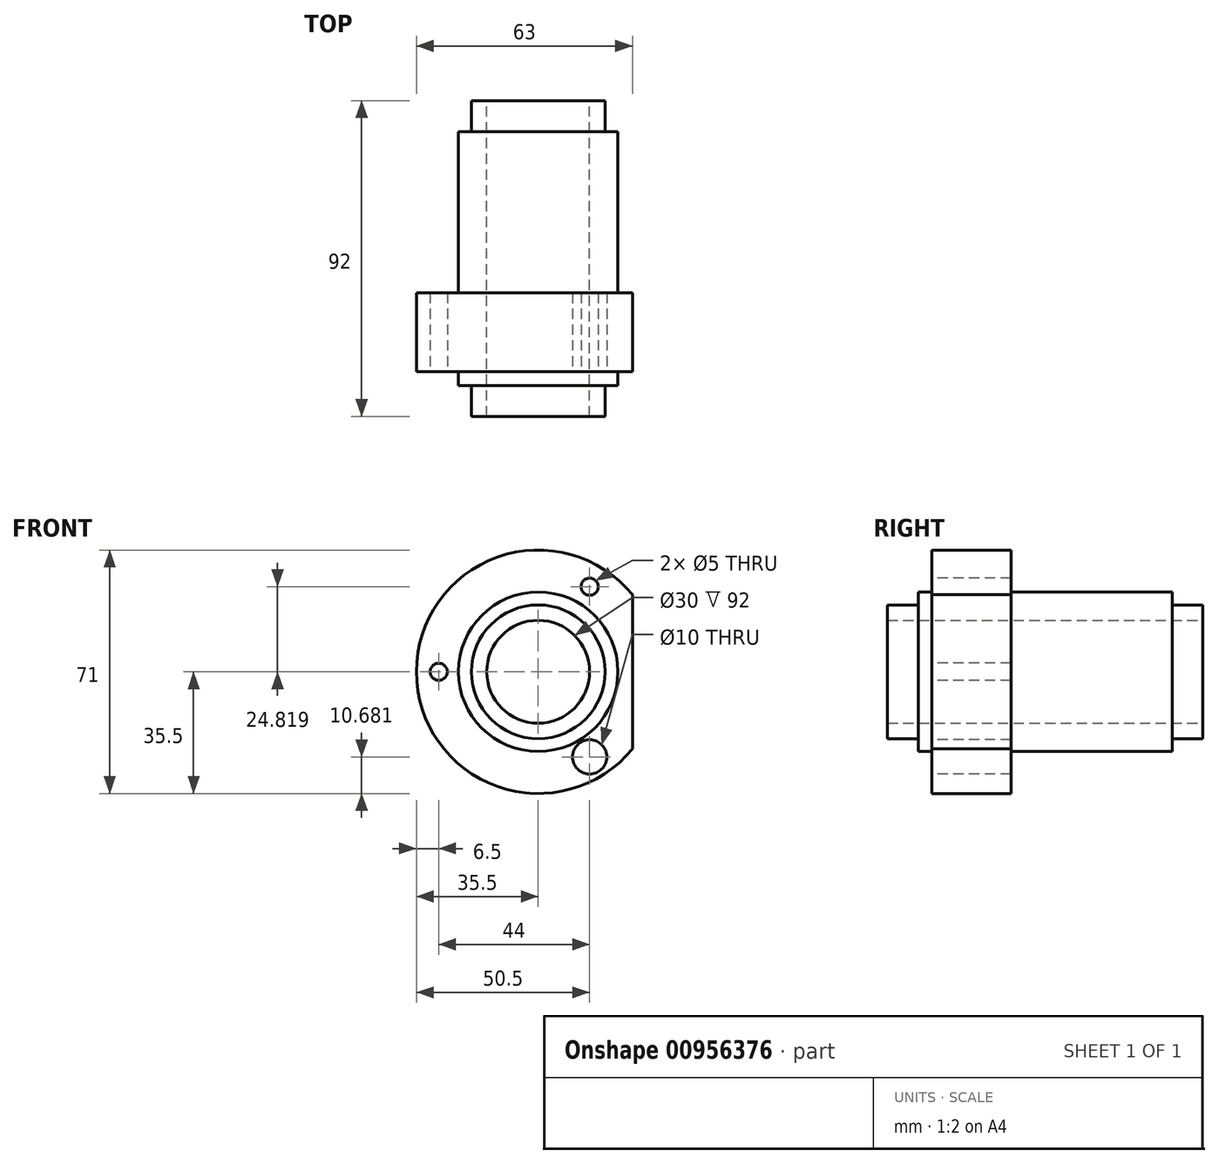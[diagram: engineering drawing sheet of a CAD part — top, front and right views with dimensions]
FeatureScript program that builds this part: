
annotation { "Feature Type Name" : "Feature", "Feature Type Description" : "" }
export const myFeature = defineFeature(function(context is Context, id is Id, definition is map)
    precondition{}
    {
        {
            var Q0;
            Q0=qCreatedBy(makeId("Front.planeOp"),FACE);
            var sketch = newSketch(context, id + "F0", { "sketchPlane" : qUnion([Q0])});
            skCircle(sketch, "E0", {"center": v(0, 0) * mm, "radius": 35.5 * mm});
            skCircle(sketch, "E1", {"center": v(0, 0) * mm, "radius": 15 * mm});
            skCircle(sketch, "E2", {"center": v(0, 0) * mm, "radius": 19.5 * mm});
            skCircle(sketch, "E3", {"center": v(0, 0) * mm, "radius": 23.25 * mm});
            skLineSegment(sketch, "E4", {"start": v(27.5, 22.45) * mm, "end": v(27.5, -22.45) * mm});
            skCircle(sketch, "E5", {"center": v(15, 24.82) * mm, "radius": 5 * mm});
            skCircle(sketch, "E6", {"center": v(15, 24.82) * mm, "radius": 2.5 * mm});
            skCircle(sketch, "E7", {"center": v(-29, 0) * mm, "radius": 5 * mm});
            skCircle(sketch, "E8", {"center": v(-29, 0) * mm, "radius": 2.5 * mm});
            skCircle(sketch, "E9.MirrorC", {"center": v(15, -24.82) * mm, "radius": 5 * mm});
            skCircle(sketch, "E10.MirrorC", {"center": v(15, -24.82) * mm, "radius": 2.5 * mm});
            skSolve(sketch);
        }
        {
            var Q0;
            Q0=makeQuery(id+"F0.imprint","IMPRINT",FACE,{"disambiguationData":[TD([[makeQuery(id+"F0.imprint","IMPRINT",EDGE,{"derivedFrom":sQuery(id+"F0.wireOp",EDGE,"E1")}),-1.0]])]});
            extrude(context, id + "F1", {"entities" : qUnion([Q0]), "depth" : 9 * mm, "offsetDistance" : 25.4 * mm});
        }
        {
            var Q0;
            Q0=makeQuery(id+"F0.imprint","IMPRINT",FACE,{"disambiguationData":[TD([[makeQuery(id+"F0.imprint","IMPRINT",EDGE,{"derivedFrom":sQuery(id+"F0.wireOp",EDGE,"E1")}),-1.0]])]});
            extrude(context, id + "F2", {"entities" : qUnion([Q0]), "operationType" : NewBodyOperationType.ADD, "oppositeDirection" : true, "depth" : 83 * mm, "offsetDistance" : 25.4 * mm});
        }
        {
            var Q0;
            Q0=makeQuery(id+"F0.imprint","IMPRINT",FACE,{"disambiguationData":[TD([[makeQuery(id+"F0.imprint","IMPRINT",EDGE,{"derivedFrom":sQuery(id+"F0.wireOp",EDGE,"E2")}),-1.0]])]});
            extrude(context, id + "F3", {"entities" : qUnion([Q0]), "operationType" : NewBodyOperationType.ADD, "oppositeDirection" : true, "depth" : 74 * mm, "offsetDistance" : 25.4 * mm});
        }
        {
            var Q0;
            Q0=makeQuery(id+"F0.imprint","IMPRINT",FACE,{"disambiguationData":[TD([[makeQuery(id+"F0.imprint","IMPRINT",EDGE,{"derivedFrom":sQuery(id+"F0.wireOp",EDGE,"E3")}),-1.0]])]});
            var Q1;
            Q1=makeQuery(id+"F0.imprint","IMPRINT",FACE,{"disambiguationData":[TD([[makeQuery(id+"F0.imprint","IMPRINT",EDGE,{"derivedFrom":sQuery(id+"F0.wireOp",EDGE,"E5")}),1.0]])]});
            var Q2;
            Q2=makeQuery(id+"F0.imprint","IMPRINT",FACE,{"disambiguationData":[TD([[makeQuery(id+"F0.imprint","IMPRINT",EDGE,{"derivedFrom":sQuery(id+"F0.wireOp",EDGE,"E6")}),1.0]])]});
            var Q3;
            Q3=makeQuery(id+"F0.imprint","IMPRINT",FACE,{"disambiguationData":[TD([[makeQuery(id+"F0.imprint","IMPRINT",EDGE,{"derivedFrom":sQuery(id+"F0.wireOp",EDGE,"E9.MirrorC")}),-1.0]])]});
            var Q4;
            Q4=makeQuery(id+"F0.imprint","IMPRINT",FACE,{"disambiguationData":[TD([[makeQuery(id+"F0.imprint","IMPRINT",EDGE,{"derivedFrom":sQuery(id+"F0.wireOp",EDGE,"E10.MirrorC")}),-1.0]])]});
            var Q5;
            Q5=makeQuery(id+"F0.imprint","IMPRINT",FACE,{"disambiguationData":[TD([[makeQuery(id+"F0.imprint","IMPRINT",EDGE,{"derivedFrom":sQuery(id+"F0.wireOp",EDGE,"E7")}),1.0]])]});
            var Q6;
            Q6=makeQuery(id+"F0.imprint","IMPRINT",FACE,{"disambiguationData":[TD([[makeQuery(id+"F0.imprint","IMPRINT",EDGE,{"derivedFrom":sQuery(id+"F0.wireOp",EDGE,"E8")}),1.0]])]});
            extrude(context, id + "F4", {"entities" : qUnion([Q0, Q1, Q2, Q3, Q4, Q5, Q6]), "operationType" : NewBodyOperationType.ADD, "oppositeDirection" : true, "depth" : 27 * mm, "offsetDistance" : 25.4 * mm});
        }
        {
            var Q0;
            Q0=makeQuery(id+"F0.imprint","IMPRINT",FACE,{"disambiguationData":[TD([[makeQuery(id+"F0.imprint","IMPRINT",EDGE,{"derivedFrom":sQuery(id+"F0.wireOp",EDGE,"E9.MirrorC")}),-1.0]])]});
            var Q1;
            Q1=makeQuery(id+"F0.imprint","IMPRINT",FACE,{"disambiguationData":[TD([[makeQuery(id+"F0.imprint","IMPRINT",EDGE,{"derivedFrom":sQuery(id+"F0.wireOp",EDGE,"E5")}),1.0]])]});
            var Q2;
            Q2=makeQuery(id+"F0.imprint","IMPRINT",FACE,{"disambiguationData":[TD([[makeQuery(id+"F0.imprint","IMPRINT",EDGE,{"derivedFrom":sQuery(id+"F0.wireOp",EDGE,"E7")}),1.0]])]});
            extrude(context, id + "F5", {"entities" : qUnion([Q0, Q1, Q2]), "operationType" : NewBodyOperationType.REMOVE, "oppositeDirection" : true, "depth" : 4 * mm, "offsetDistance" : 25.4 * mm});
        }
        {
            var Q0;
            Q0=makeQuery(id+"F0.imprint","IMPRINT",FACE,{"disambiguationData":[TD([[makeQuery(id+"F0.imprint","IMPRINT",EDGE,{"derivedFrom":sQuery(id+"F0.wireOp",EDGE,"E10.MirrorC")}),-1.0]])]});
            var Q1;
            Q1=makeQuery(id+"F0.imprint","IMPRINT",FACE,{"disambiguationData":[TD([[makeQuery(id+"F0.imprint","IMPRINT",EDGE,{"derivedFrom":sQuery(id+"F0.wireOp",EDGE,"E6")}),1.0]])]});
            var Q2;
            Q2=makeQuery(id+"F0.imprint","IMPRINT",FACE,{"disambiguationData":[TD([[makeQuery(id+"F0.imprint","IMPRINT",EDGE,{"derivedFrom":sQuery(id+"F0.wireOp",EDGE,"E8")}),1.0]])]});
            extrude(context, id + "F6", {"entities" : qUnion([Q0, Q1, Q2]), "operationType" : NewBodyOperationType.REMOVE, "oppositeDirection" : true, "depth" : 27 * mm, "offsetDistance" : 25.4 * mm});
        }
    });
